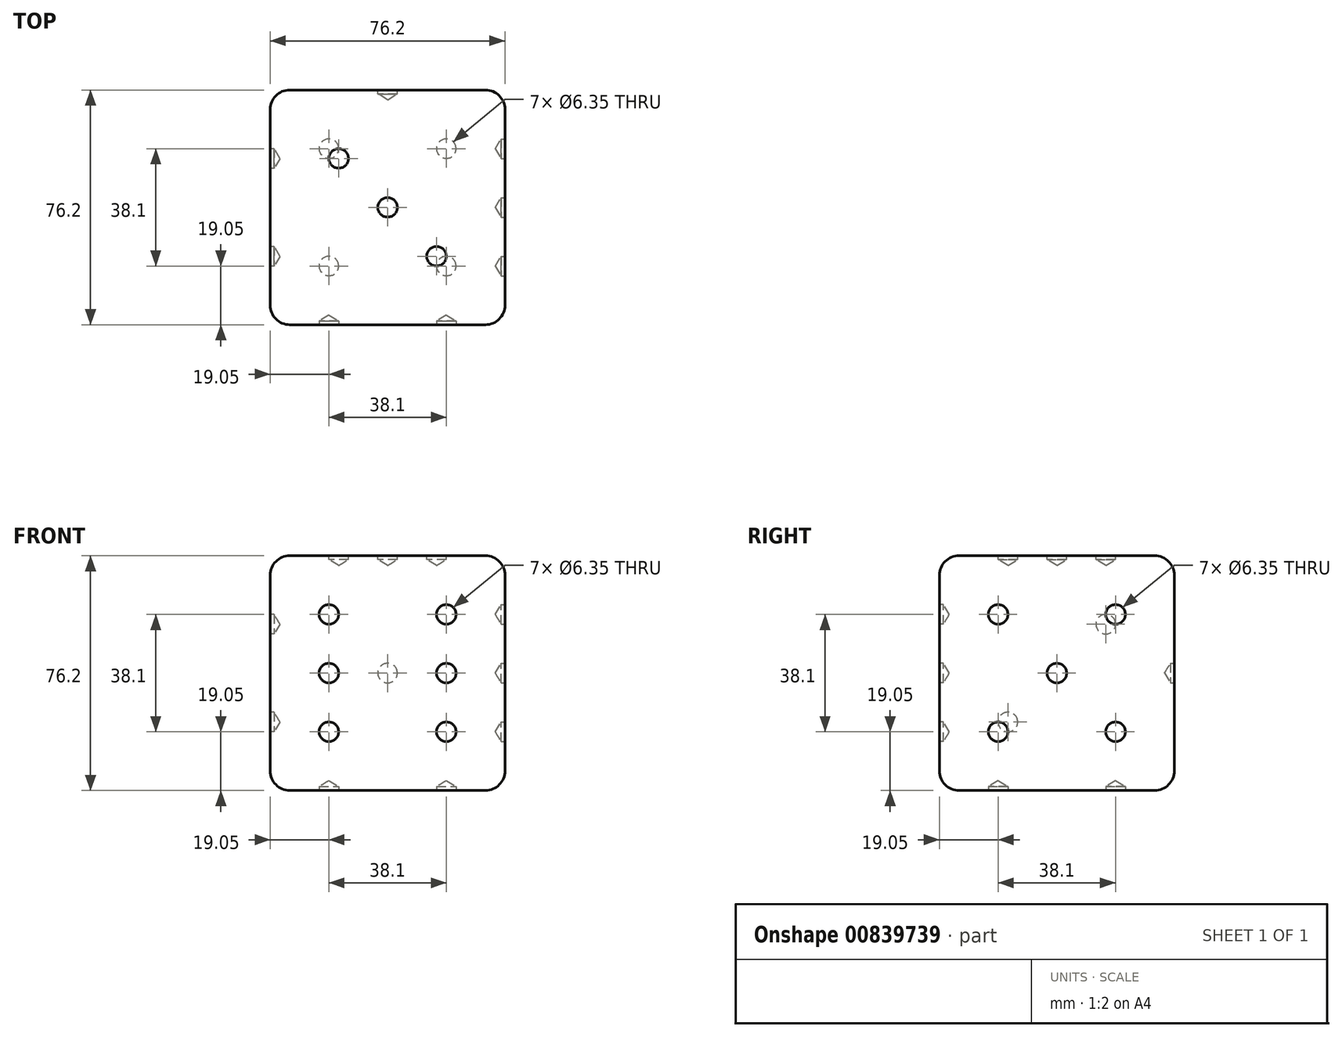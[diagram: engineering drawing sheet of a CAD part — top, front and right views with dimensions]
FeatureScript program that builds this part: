
annotation { "Feature Type Name" : "Feature", "Feature Type Description" : "" }
export const myFeature = defineFeature(function(context is Context, id is Id, definition is map)
    precondition{}
    {
        {
            var Q0;
            Q0=qCreatedBy(makeId("Front.planeOp"),FACE);
            var sketch = newSketch(context, id + "F0", { "sketchPlane" : qUnion([Q0])});
            skLineSegment(sketch, "E0.bottom", {"start": v(38.1, 38.1) * mm, "end": v(-38.1, 38.1) * mm});
            skLineSegment(sketch, "E0.top", {"start": v(38.1, -38.1) * mm, "end": v(-38.1, -38.1) * mm});
            skLineSegment(sketch, "E0.left", {"start": v(38.1, 38.1) * mm, "end": v(38.1, -38.1) * mm});
            skLineSegment(sketch, "E0.right", {"start": v(-38.1, 38.1) * mm, "end": v(-38.1, -38.1) * mm});
            skPoint(sketch, "E0.middle", {"position": v(0, 0) * mm});
            skSolve(sketch);
        }
        {
            var Q0;
            Q0 = qSketchRegion(id + "F0", true);
            extrude(context, id + "F1", {"entities" : qUnion([Q0]), "endBound" : BoundingType.SYMMETRIC, "depth" : 76.2 * mm, "offsetDistance" : 25.4 * mm});
        }
        {
            var Q0;
            Q0=makeQuery(id+"F1.opExtrude","CAP_EDGE",EDGE,{"disambiguationData":[OSD([sQuery(id+"F0.wireOp",EDGE,"E0.bottom")])],"isStart":false});
            var Q1;
            Q1=makeQuery(id+"F1.opExtrude","SWEPT_EDGE",EDGE,{"disambiguationData":[OSD([sQuery(id+"F0.wireOp",EDGE,"E0.bottom"),sQuery(id+"F0.wireOp",EDGE,"E0.right")])]});
            var Q2;
            Q2=makeQuery(id+"F1.opExtrude","CAP_EDGE",EDGE,{"disambiguationData":[OSD([sQuery(id+"F0.wireOp",EDGE,"E0.right")])],"isStart":false});
            var Q3;
            Q3=makeQuery(id+"F1.opExtrude","CAP_EDGE",EDGE,{"disambiguationData":[OSD([sQuery(id+"F0.wireOp",EDGE,"E0.left")])],"isStart":false});
            var Q4;
            Q4=makeQuery(id+"F1.opExtrude","SWEPT_EDGE",EDGE,{"disambiguationData":[OSD([sQuery(id+"F0.wireOp",EDGE,"E0.bottom"),sQuery(id+"F0.wireOp",EDGE,"E0.left")])]});
            var Q5;
            Q5=makeQuery(id+"F1.opExtrude","CAP_EDGE",EDGE,{"disambiguationData":[OSD([sQuery(id+"F0.wireOp",EDGE,"E0.left")])],"isStart":true});
            var Q6;
            Q6=makeQuery(id+"F1.opExtrude","SWEPT_EDGE",EDGE,{"disambiguationData":[OSD([sQuery(id+"F0.wireOp",EDGE,"E0.top"),sQuery(id+"F0.wireOp",EDGE,"E0.left")])]});
            var Q7;
            Q7=makeQuery(id+"F1.opExtrude","CAP_EDGE",EDGE,{"disambiguationData":[OSD([sQuery(id+"F0.wireOp",EDGE,"E0.top")])],"isStart":true});
            var Q8;
            Q8=makeQuery(id+"F1.opExtrude","CAP_EDGE",EDGE,{"disambiguationData":[OSD([sQuery(id+"F0.wireOp",EDGE,"E0.top")])],"isStart":false});
            var Q9;
            Q9=makeQuery(id+"F1.opExtrude","SWEPT_EDGE",EDGE,{"disambiguationData":[OSD([sQuery(id+"F0.wireOp",EDGE,"E0.top"),sQuery(id+"F0.wireOp",EDGE,"E0.right")])]});
            var Q10;
            Q10=makeQuery(id+"F1.opExtrude","CAP_EDGE",EDGE,{"disambiguationData":[OSD([sQuery(id+"F0.wireOp",EDGE,"E0.right")])],"isStart":true});
            var Q11;
            Q11=makeQuery(id+"F1.opExtrude","CAP_EDGE",EDGE,{"disambiguationData":[OSD([sQuery(id+"F0.wireOp",EDGE,"E0.bottom")])],"isStart":true});
            fillet(context, id + "F2", {"entities" : qUnion([Q0, Q1, Q2, Q3, Q4, Q5, Q6, Q7, Q8, Q9, Q10, Q11]), "radius" : 6.35 * mm, "tangentPropagation" : true, "allowEdgeOverflow" : false});
        }
        {
            var Q0;
            Q0=makeQuery(id+"F1.opExtrude","CAP_FACE",FACE,{"disambiguationData":[OSD([sQuery(id+"F0.wireOp",EDGE,"E0.bottom"),sQuery(id+"F0.wireOp",EDGE,"E0.top"),sQuery(id+"F0.wireOp",EDGE,"E0.left"),sQuery(id+"F0.wireOp",EDGE,"E0.right")])],"isStart":false});
            var sketch = newSketch(context, id + "F3", { "sketchPlane" : qUnion([Q0])});
            skLineSegment(sketch, "E1.bottom", {"start": v(19.05, 19.05) * mm, "end": v(-19.05, 19.05) * mm});
            skLineSegment(sketch, "E1.top", {"start": v(19.05, -19.05) * mm, "end": v(-19.05, -19.05) * mm});
            skLineSegment(sketch, "E1.left", {"start": v(19.05, 19.05) * mm, "end": v(19.05, -19.05) * mm});
            skLineSegment(sketch, "E1.right", {"start": v(-19.05, 19.05) * mm, "end": v(-19.05, -19.05) * mm});
            skPoint(sketch, "E1.middle", {"position": v(0, 0) * mm});
            skPoint(sketch, "E2", {"position": v(-19.05, 0) * mm});
            skPoint(sketch, "E3", {"position": v(19.05, 0) * mm});
            skSolve(sketch);
        }
        {
            var Q0;
            Q0=sQuery(id+"F3.wireOp",VERTEX,"E2");
            var Q1;
            Q1=sQuery(id+"F3.wireOp",VERTEX,"E1.bottom.end");
            var Q2;
            Q2=sQuery(id+"F3.wireOp",VERTEX,"E1.bottom.start");
            var Q3;
            Q3=sQuery(id+"F3.wireOp",VERTEX,"E3");
            var Q4;
            Q4=sQuery(id+"F3.wireOp",VERTEX,"E1.top.start");
            var Q5;
            Q5=sQuery(id+"F3.wireOp",VERTEX,"E1.top.end");
            var Q6;
            Q6=makeQuery(id+"F1.opExtrude","SWEPT_BODY",BODY,{"disambiguationData":[OSD([sQuery(id+"F0.wireOp",EDGE,"E0.bottom"),sQuery(id+"F0.wireOp",EDGE,"E0.top"),sQuery(id+"F0.wireOp",EDGE,"E0.left"),sQuery(id+"F0.wireOp",EDGE,"E0.right")])]});
            hole(context, id + "F4", {"style" : HoleStyle.SIMPLE, "endStyle" : HoleEndStyle.BLIND, "holeDiameter" : 6.35 * mm, "majorDiameter" : 6.35 * mm, "holeDepth" : 1.27 * mm, "isTappedThrough" : true, "tappedDepth" : 12.7 * mm, "tapClearance" : 3, "locations" : qUnion([Q0, Q1, Q2, Q3, Q4, Q5]), "scope" : qUnion([Q6])});
        }
        {
            var Q0;
            Q0=makeQuery(id+"F1.opExtrude","CAP_FACE",FACE,{"disambiguationData":[OSD([sQuery(id+"F0.wireOp",EDGE,"E0.bottom"),sQuery(id+"F0.wireOp",EDGE,"E0.top"),sQuery(id+"F0.wireOp",EDGE,"E0.left"),sQuery(id+"F0.wireOp",EDGE,"E0.right")])],"isStart":true});
            var sketch = newSketch(context, id + "F5", { "sketchPlane" : qUnion([Q0])});
            skPoint(sketch, "E4", {"position": v(0, 0) * mm});
            skSolve(sketch);
        }
        {
            var Q0;
            Q0=sQuery(id+"F5.wireOp",VERTEX,"E4");
            var Q1;
            Q1=makeQuery(id+"F1.opExtrude","SWEPT_BODY",BODY,{"disambiguationData":[OSD([sQuery(id+"F0.wireOp",EDGE,"E0.bottom"),sQuery(id+"F0.wireOp",EDGE,"E0.top"),sQuery(id+"F0.wireOp",EDGE,"E0.left"),sQuery(id+"F0.wireOp",EDGE,"E0.right")])]});
            hole(context, id + "F6", {"style" : HoleStyle.SIMPLE, "endStyle" : HoleEndStyle.BLIND, "holeDiameter" : 6.35 * mm, "majorDiameter" : 6.35 * mm, "holeDepth" : 1.27 * mm, "isTappedThrough" : true, "tappedDepth" : 12.7 * mm, "tapClearance" : 3, "locations" : qUnion([Q0]), "scope" : qUnion([Q1])});
        }
        {
            var Q0;
            Q0=makeQuery(id+"F1.opExtrude","SWEPT_FACE",FACE,{"disambiguationData":[OSD([sQuery(id+"F0.wireOp",EDGE,"E0.left")])]});
            var sketch = newSketch(context, id + "F7", { "sketchPlane" : qUnion([Q0])});
            skLineSegment(sketch, "E5.bottom", {"start": v(19.05, 19.05) * mm, "end": v(-19.05, 19.05) * mm});
            skLineSegment(sketch, "E5.top", {"start": v(19.05, -19.05) * mm, "end": v(-19.05, -19.05) * mm});
            skLineSegment(sketch, "E5.left", {"start": v(19.05, 19.05) * mm, "end": v(19.05, -19.05) * mm});
            skLineSegment(sketch, "E5.right", {"start": v(-19.05, 19.05) * mm, "end": v(-19.05, -19.05) * mm});
            skPoint(sketch, "E5.middle", {"position": v(0, 0) * mm});
            skSolve(sketch);
        }
        {
            var Q0;
            Q0=sQuery(id+"F7.wireOp",VERTEX,"E5.bottom.end");
            var Q1;
            Q1=sQuery(id+"F7.wireOp",VERTEX,"E5.middle");
            var Q2;
            Q2=sQuery(id+"F7.wireOp",VERTEX,"E5.bottom.start");
            var Q3;
            Q3=sQuery(id+"F7.wireOp",VERTEX,"E5.top.start");
            var Q4;
            Q4=sQuery(id+"F7.wireOp",VERTEX,"E5.top.end");
            var Q5;
            Q5=makeQuery(id+"F1.opExtrude","SWEPT_BODY",BODY,{"disambiguationData":[OSD([sQuery(id+"F0.wireOp",EDGE,"E0.bottom"),sQuery(id+"F0.wireOp",EDGE,"E0.top"),sQuery(id+"F0.wireOp",EDGE,"E0.left"),sQuery(id+"F0.wireOp",EDGE,"E0.right")])]});
            hole(context, id + "F8", {"style" : HoleStyle.SIMPLE, "endStyle" : HoleEndStyle.BLIND, "holeDiameter" : 6.35 * mm, "majorDiameter" : 6.35 * mm, "holeDepth" : 1.27 * mm, "isTappedThrough" : true, "tappedDepth" : 12.7 * mm, "tapClearance" : 3, "locations" : qUnion([Q0, Q1, Q2, Q3, Q4]), "scope" : qUnion([Q5])});
        }
        {
            var Q0;
            Q0=makeQuery(id+"F1.opExtrude","SWEPT_FACE",FACE,{"disambiguationData":[OSD([sQuery(id+"F0.wireOp",EDGE,"E0.right")])]});
            var sketch = newSketch(context, id + "F9", { "sketchPlane" : qUnion([Q0])});
            skLineSegment(sketch, "E6", {"start": v(-31.75, 31.75) * mm, "end": v(31.75, -31.75) * mm});
            skLineSegment(sketch, "E7", {"start": v(31.75, -31.75) * mm, "end": v(-31.75, 31.75) * mm});
            skLineSegment(sketch, "E8", {"start": v(0, 31.75) * mm, "end": v(-31.75, 0) * mm});
            skLineSegment(sketch, "E9", {"start": v(-31.75, 0) * mm, "end": v(0, 31.75) * mm});
            skLineSegment(sketch, "E10", {"start": v(31.75, 0) * mm, "end": v(0, -31.75) * mm});
            skLineSegment(sketch, "E11", {"start": v(0, -31.75) * mm, "end": v(31.75, 0) * mm});
            skPoint(sketch, "E12", {"position": v(-15.87, 15.88) * mm});
            skPoint(sketch, "E13", {"position": v(15.88, -15.88) * mm});
            skSolve(sketch);
        }
        {
            var Q0;
            Q0=sQuery(id+"F9.wireOp",VERTEX,"E12");
            var Q1;
            Q1=sQuery(id+"F9.wireOp",VERTEX,"E13");
            var Q2;
            Q2=makeQuery(id+"F1.opExtrude","SWEPT_BODY",BODY,{"disambiguationData":[OSD([sQuery(id+"F0.wireOp",EDGE,"E0.bottom"),sQuery(id+"F0.wireOp",EDGE,"E0.top"),sQuery(id+"F0.wireOp",EDGE,"E0.left"),sQuery(id+"F0.wireOp",EDGE,"E0.right")])]});
            hole(context, id + "F10", {"style" : HoleStyle.SIMPLE, "endStyle" : HoleEndStyle.BLIND, "holeDiameter" : 6.35 * mm, "majorDiameter" : 6.35 * mm, "holeDepth" : 1.27 * mm, "isTappedThrough" : true, "tappedDepth" : 12.7 * mm, "tapClearance" : 3, "locations" : qUnion([Q0, Q1]), "scope" : qUnion([Q2])});
        }
        {
            var Q0;
            Q0=makeQuery(id+"F1.opExtrude","SWEPT_FACE",FACE,{"disambiguationData":[OSD([sQuery(id+"F0.wireOp",EDGE,"E0.bottom")])]});
            var sketch = newSketch(context, id + "F11", { "sketchPlane" : qUnion([Q0])});
            skLineSegment(sketch, "E14", {"start": v(-31.75, 31.75) * mm, "end": v(31.75, -31.75) * mm});
            skLineSegment(sketch, "E15", {"start": v(0, 31.75) * mm, "end": v(-31.75, 0) * mm});
            skLineSegment(sketch, "E16", {"start": v(31.75, 0) * mm, "end": v(0, -31.75) * mm});
            skPoint(sketch, "E17", {"position": v(-15.88, 15.87) * mm});
            skPoint(sketch, "E18", {"position": v(0, 0) * mm});
            skPoint(sketch, "E19", {"position": v(15.87, -15.88) * mm});
            skSolve(sketch);
        }
        {
            var Q0;
            Q0=sQuery(id+"F11.wireOp",VERTEX,"E17");
            var Q1;
            Q1=sQuery(id+"F11.wireOp",VERTEX,"E18");
            var Q2;
            Q2=sQuery(id+"F11.wireOp",VERTEX,"E19");
            var Q3;
            Q3=makeQuery(id+"F1.opExtrude","SWEPT_BODY",BODY,{"disambiguationData":[OSD([sQuery(id+"F0.wireOp",EDGE,"E0.bottom"),sQuery(id+"F0.wireOp",EDGE,"E0.top"),sQuery(id+"F0.wireOp",EDGE,"E0.left"),sQuery(id+"F0.wireOp",EDGE,"E0.right")])]});
            hole(context, id + "F12", {"style" : HoleStyle.SIMPLE, "endStyle" : HoleEndStyle.BLIND, "holeDiameter" : 6.35 * mm, "majorDiameter" : 6.35 * mm, "holeDepth" : 1.27 * mm, "isTappedThrough" : true, "tappedDepth" : 12.7 * mm, "tapClearance" : 3, "locations" : qUnion([Q0, Q1, Q2]), "scope" : qUnion([Q3])});
        }
        {
            var Q0;
            Q0=makeQuery(id+"F1.opExtrude","SWEPT_FACE",FACE,{"disambiguationData":[OSD([sQuery(id+"F0.wireOp",EDGE,"E0.top")])]});
            var sketch = newSketch(context, id + "F13", { "sketchPlane" : qUnion([Q0])});
            skLineSegment(sketch, "E20.bottom", {"start": v(19.05, 19.05) * mm, "end": v(-19.05, 19.05) * mm});
            skLineSegment(sketch, "E20.top", {"start": v(19.05, -19.05) * mm, "end": v(-19.05, -19.05) * mm});
            skLineSegment(sketch, "E20.left", {"start": v(19.05, 19.05) * mm, "end": v(19.05, -19.05) * mm});
            skLineSegment(sketch, "E20.right", {"start": v(-19.05, 19.05) * mm, "end": v(-19.05, -19.05) * mm});
            skPoint(sketch, "E20.middle", {"position": v(0, 0) * mm});
            skSolve(sketch);
        }
        {
            var Q0;
            Q0=sQuery(id+"F13.wireOp",VERTEX,"E20.bottom.end");
            var Q1;
            Q1=sQuery(id+"F13.wireOp",VERTEX,"E20.bottom.start");
            var Q2;
            Q2=sQuery(id+"F13.wireOp",VERTEX,"E20.top.start");
            var Q3;
            Q3=sQuery(id+"F13.wireOp",VERTEX,"E20.top.end");
            var Q4;
            Q4=makeQuery(id+"F1.opExtrude","SWEPT_BODY",BODY,{"disambiguationData":[OSD([sQuery(id+"F0.wireOp",EDGE,"E0.bottom"),sQuery(id+"F0.wireOp",EDGE,"E0.top"),sQuery(id+"F0.wireOp",EDGE,"E0.left"),sQuery(id+"F0.wireOp",EDGE,"E0.right")])]});
            hole(context, id + "F14", {"style" : HoleStyle.SIMPLE, "endStyle" : HoleEndStyle.BLIND, "holeDiameter" : 6.35 * mm, "majorDiameter" : 6.35 * mm, "holeDepth" : 1.27 * mm, "isTappedThrough" : true, "tappedDepth" : 12.7 * mm, "tapClearance" : 3, "locations" : qUnion([Q0, Q1, Q2, Q3]), "scope" : qUnion([Q4])});
        }
    });
